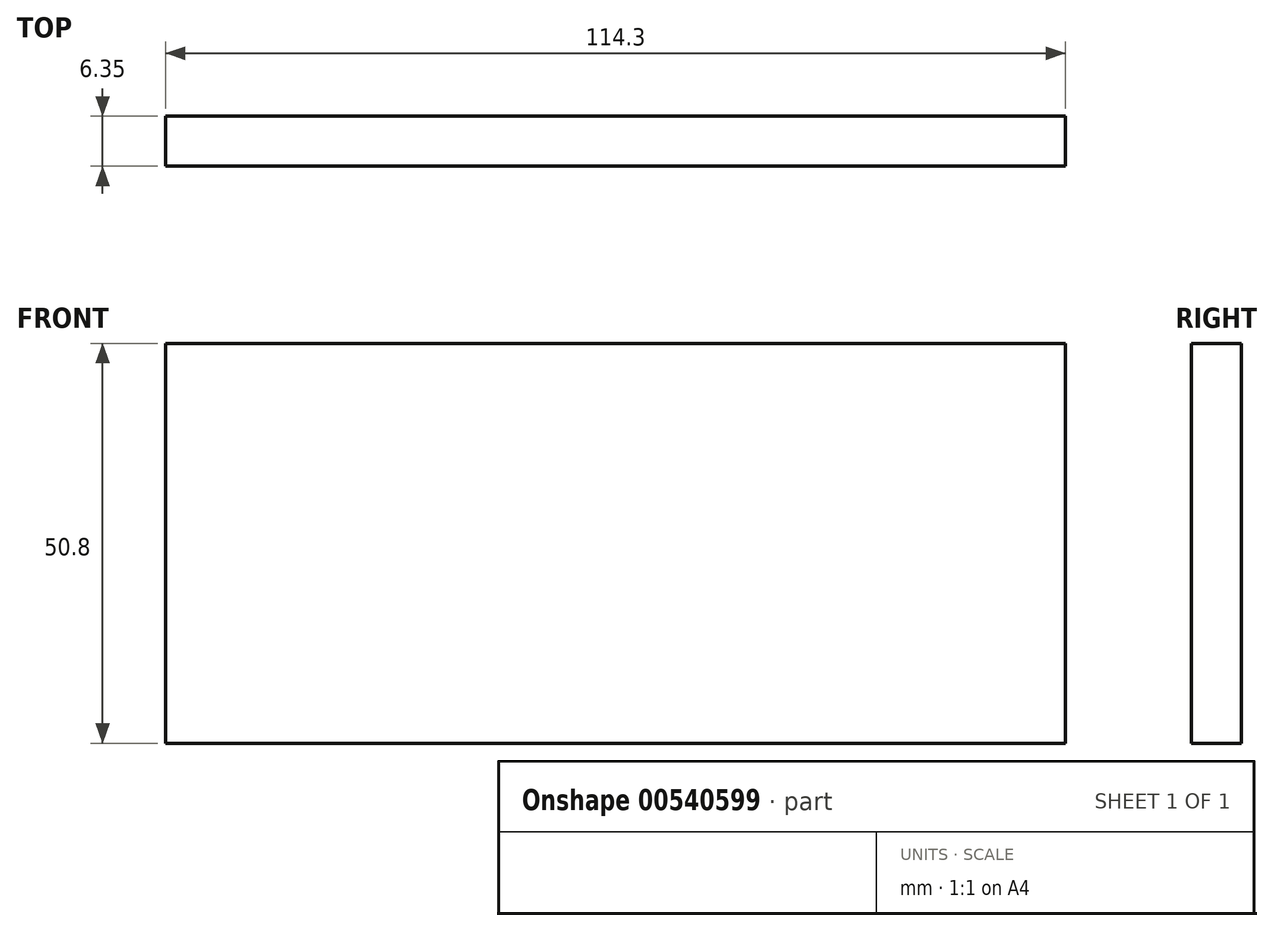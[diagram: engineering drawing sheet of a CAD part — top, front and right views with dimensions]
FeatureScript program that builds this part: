
annotation { "Feature Type Name" : "Feature", "Feature Type Description" : "" }
export const myFeature = defineFeature(function(context is Context, id is Id, definition is map)
    precondition{}
    {
        {
            var Q0;
            Q0=qCreatedBy(makeId("Front.planeOp"),FACE);
            var sketch = newSketch(context, id + "F0", { "sketchPlane" : qUnion([Q0])});
            skLineSegment(sketch, "E0.bottom", {"start": v(0, 0) * mm, "end": v(114.3, 0) * mm});
            skLineSegment(sketch, "E0.top", {"start": v(0, 50.8) * mm, "end": v(114.3, 50.8) * mm});
            skLineSegment(sketch, "E0.left", {"start": v(0, 0) * mm, "end": v(0, 50.8) * mm});
            skLineSegment(sketch, "E0.right", {"start": v(114.3, 0) * mm, "end": v(114.3, 50.8) * mm});
            skSolve(sketch);
        }
        {
            var Q0;
            Q0=makeQuery(id+"F0.imprint","IMPRINT",FACE,{"disambiguationData":[TD([[makeQuery(id+"F0.imprint","IMPRINT",EDGE,{"derivedFrom":sQuery(id+"F0.wireOp",EDGE,"E0.bottom")}),1.0]])]});
            extrude(context, id + "F1", {"entities" : qUnion([Q0]), "depth" : 6.35 * mm, "offsetDistance" : 25.4 * mm});
        }
    });
